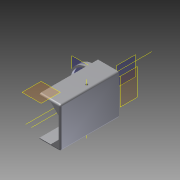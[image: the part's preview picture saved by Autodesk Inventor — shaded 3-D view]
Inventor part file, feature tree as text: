
AUTODESK INVENTOR PART (.ipt)
format: ipt  version: 2012 (Build 160160000, 160)  size: 837,632 bytes
history: native  units: mm
features: sketch x31, extrude x31, reference x30, projected_geometry x23, fillet x12, plane x5, other x4
ambient origin geometry x8: Origin, YZ Plane, XZ Plane, XY Plane, X Axis, Y Axis, Z Axis, Center Point
bodies: Solid1 (feature_tree)
feature tree (136):
  plane  "Work Plane2"
  sketch  "Sketch3"  dims[d1=0.3mm d2=0.3mm]
  plane  "Work Plane3"
  extrude  "Extrusion1"  Depth=0.3mm
  extrude  "Extrusion2"  Depth=10.0mm TaperAngle=0.0deg
  plane  "Work Plane4"
  extrude  "Extrusion3"  Depth=10.0mm TaperAngle=0.0deg
  extrude  "Extrusion4"  Depth=2.0mm
  extrude  "Extrusion5"  Depth=2.0mm
  extrude  "Extrusion6"  Depth=2.0mm TaperAngle=0.0deg
  extrude  "Extrusion7"  TaperAngle=0.0deg  [1 undecoded]
  extrude  "Extrusion8"  TaperAngle=0.0deg  [1 undecoded]
  fillet  "Fillet3"  Radius=20.0mm
  fillet  "Fillet4"  Radius=20.0mm
  fillet  "Fillet5"  Radius=0.3mm
  extrude  "Extrusion10"  Depth=0.3mm
  extrude  "Extrusion11"  Depth=0.3mm TaperAngle=0.0deg
  extrude  "Extrusion12"  Depth=1.0mm
  extrude  "Extrusion13"  Depth=2.0mm TaperAngle=0.0deg
  extrude  "Extrusion14"  Depth=0.3mm
  extrude  "Extrusion15"  Depth=0.3mm
  extrude  "Extrusion16"  TaperAngle=0.0deg  [1 undecoded]
  extrude  "Extrusion17"  Depth=2.0mm
  extrude  "Extrusion18"  Depth=2.0mm TaperAngle=0.0deg
  extrude  "Extrusion20"  Depth=14.0mm
  extrude  "Extrusion21"  Depth=7.0mm TaperAngle=0.0deg
  plane  "Work Plane5"
  extrude  "Extrusion22"  Depth=3.3mm
  extrude  "Extrusion23"  Depth=3.3mm
  extrude  "Extrusion24"  Depth=0.3mm
  extrude  "Extrusion25"  Depth=0.3mm
  plane  "Work Plane7"
  extrude  "Extrusion26"  Depth=20.0mm TaperAngle=0.0deg
  extrude  "Extrusion27"  Depth=0.3mm
  extrude  "Extrusion28"  Depth=0.3mm
  extrude  "Extrusion29"  Depth=2.0mm
  extrude  "Extrusion30"  Depth=2.0mm
  extrude  "Extrusion31"  TaperAngle=45.0deg  [1 undecoded]
  extrude  "Extrusion34"  Depth=9.0mm
  other  "Work Axis2"
  fillet  "Fillet47"  Radius=10.0mm
  fillet  "Fillet48"  [1 undecoded]
  fillet  "Fillet49"  Radius=10.0mm
  fillet  "Fillet50"  Radius=10.0mm
  fillet  "Fillet51"  Radius=10.0mm
  fillet  "Fillet52"  Radius=0.3mm
  fillet  "Fillet53"  Radius=0.3mm
  fillet  "Fillet54"  Radius=10.0mm
  fillet  "Fillet55"  Radius=10.0mm
  other  "Work Axis3"
  extrude  "Extrusion35"  Depth=4.0mm
  other  "Work Axis4"
  other  "Work Axis5"
  reference  "Reference32"
  sketch  "Sketch4"  dims[d3=2.0mm d4=10.0mm d5=0.0mm]
  reference  "Reference33"
  sketch  "Sketch5"  dims[d6=0.3mm d7=10.0mm d8=0.0mm]
  sketch  "Sketch7"  dims[d9=2.0mm d10=2.0mm]
  projected_geometry  "Projected Loop3"
  sketch  "Sketch8"  dims[d11=2.0mm d12=2.0mm]
  sketch  "Sketch10"  dims[d13=120.0mm d14=2.0mm d15=0.0mm]
  reference  "Reference36"
  sketch  "Sketch11"  dims[d24=2.0mm d25=0.0mm]
  reference  "Reference37"
  sketch  "Sketch12"  dims[d26=2.0mm d27=0.0mm d28=20.0mm d29=0.0mm d31=20.0mm d32=0.0mm d34=0.3mm]
  sketch  "Sketch15"  dims[d35=20.0mm d36=0.0mm d37=0.3mm]
  projected_geometry  "Projected Loop5"
  projected_geometry  "Projected Loop6"
  sketch  "Sketch16"  dims[d38=10.0mm d39=0.0mm d40=0.3mm d41=0.0mm]
  reference  "Reference46"
  reference  "Reference47"
  reference  "Reference48"
  reference  "Reference49"
  reference  "Reference50"
  reference  "Reference51"
  reference  "Reference52"
  reference  "Reference53"
  sketch  "Sketch17"  dims[d43=1.0mm d44=1.0mm]
  reference  "Reference54"
  reference  "Reference55"
  reference  "Reference56"
  reference  "Reference57"
  reference  "Reference58"
  reference  "Reference59"
  reference  "Reference60"
  reference  "Reference61"
  sketch  "Sketch18"  dims[d45=1.0mm d52=2.0mm d53=0.0mm]
  reference  "Reference62"
  sketch  "Sketch19"  dims[d58=2.0mm d59=0.0mm d60=0.3mm]
  projected_geometry  "Projected Loop7"
  projected_geometry  "Projected Loop8"
  sketch  "Sketch20"  dims[d61=0.3mm d62=0.3mm]
  projected_geometry  "Projected Loop9"
  projected_geometry  "Projected Loop10"
  sketch  "Sketch21"  dims[d63=0.3mm d64=0.0mm]
  projected_geometry  "Projected Loop11"
  sketch  "Sketch22"  dims[d66=0.0mm d67=2.0mm]
  reference  "Reference63"
  reference  "Reference64"
  reference  "Reference65"
  reference  "Reference66"
  reference  "Reference67"
  reference  "Reference68"
  reference  "Reference69"
  reference  "Reference70"
  sketch  "Sketch23"  dims[d68=2.0mm d69=2.0mm d70=0.0mm]
  projected_geometry  "Projected Loop12"
  projected_geometry  "Projected Loop13"
  projected_geometry  "Projected Loop14"
  projected_geometry  "Projected Loop15"
  sketch  "Sketch25"  dims[d72=2.0mm d73=0.0mm d74=14.0mm]
  projected_geometry  "Projected Loop16"
  sketch  "Sketch26"  dims[d78=2.0mm d79=0.0mm d80=7.0mm d81=0.0mm]
  sketch  "Sketch28"  dims[d82=10.0mm d83=0.0mm d84=3.3mm]
  projected_geometry  "Projected Loop21"
  sketch  "Sketch29"  dims[d85=3.3mm d86=3.3mm]
  projected_geometry  "Projected Loop22"
  projected_geometry  "Projected Loop23"
  sketch  "Sketch30"  dims[d87=3.3mm d88=0.3mm]
  projected_geometry  "Projected Loop24"
  sketch  "Sketch31"  dims[d89=0.3mm d90=0.3mm]
  projected_geometry  "Projected Loop25"
  sketch  "Sketch32"  dims[d91=0.3mm d94=20.0mm d95=0.0mm]
  sketch  "Sketch33"  dims[d97=0.3mm d98=0.3mm]
  projected_geometry  "Projected Loop26"
  sketch  "Sketch34"  dims[d99=0.3mm d100=0.3mm]
  projected_geometry  "Projected Loop27"
  sketch  "Sketch35"  dims[d101=0.3mm d102=0.0mm d103=2.0mm]
  projected_geometry  "Projected Loop28"
  projected_geometry  "Projected Loop29"
  sketch  "Sketch37"  dims[d104=2.0mm d105=2.0mm]
  sketch  "Sketch38"  dims[d106=2.0mm d111=45.0deg]
  projected_geometry  "Projected Loop31"
  sketch  "Sketch41"  dims[d112=9.0mm d113=9.0mm d114=10.0mm d115=0.0mm d116=0.0mm d117=0.0mm d123=10.0mm d124=0.0mm d132=10.0mm d133=0.0mm d134=10.0mm d135=0.0mm d138=0.3mm d139=0.0mm d151=0.3mm d152=0.0mm d153=10.0mm d154=0.0mm d155=10.0mm d156=0.0mm]
  reference  "Reference73"
  sketch  "Sketch42"  dims[d157=10.0mm d158=0.0mm d159=4.0mm d160=10.0mm d161=0.0mm d162=10.0mm d163=0.0mm d186=25.4mm d187=0.0mm d189=1.0mm d190=2.0mm d191=2.0mm d192=2.0mm d193=2.0mm d194=1.0mm d195=2.0mm d196=2.0mm d197=1.5mm d198=78.5mm d199=0.0mm]
note: 5 required parameter values undecoded (feature->parameter linkage not recoverable at this tier; creation-order binding heuristic only, values carry confidence <= 0.55)
